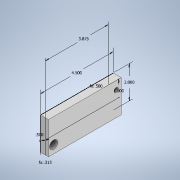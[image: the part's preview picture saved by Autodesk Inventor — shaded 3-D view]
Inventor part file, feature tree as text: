
AUTODESK INVENTOR PART (.ipt)
format: ipt  version: 2021 (Build 250183000, 183)  size: 110,080 bytes
history: native  units: in
note: dims shown in document units (in); Inventor stores cm internally (conversion verified against a paired STEP export)
features: hole x2, sketch x1, extrude x1
ambient origin geometry x8: Origin, YZ Plane, XZ Plane, XY Plane, X Axis, Y Axis, Z Axis, Center Point
bodies: Solid1 (feature_tree)
feature tree (4):
  sketch  "Sketch2"  dims[d0=2.0in d1=4.5in d2=3.875in d3=1.0in d4=0.5in d5=0.3125in d6=0.5in d7=0.0in d8=0.25in d9=0.75in d10=0.375in d11=0.25in d12=0.5635in d13=0.75in d14=0.8108in d15=0.5in d16=0.5in d17=0.75in d18=0.375in d19=0.25in d20=0.5635in d21=0.75in d22=0.8108in]
  extrude  "Extrusion1"  Depth=4.5in
  hole  "Hole1"  [1 undecoded]
  hole  "Hole2"  [1 undecoded]
note: 2 required parameter values undecoded (feature->parameter linkage not recoverable at this tier; creation-order binding heuristic only, values carry confidence <= 0.55)
